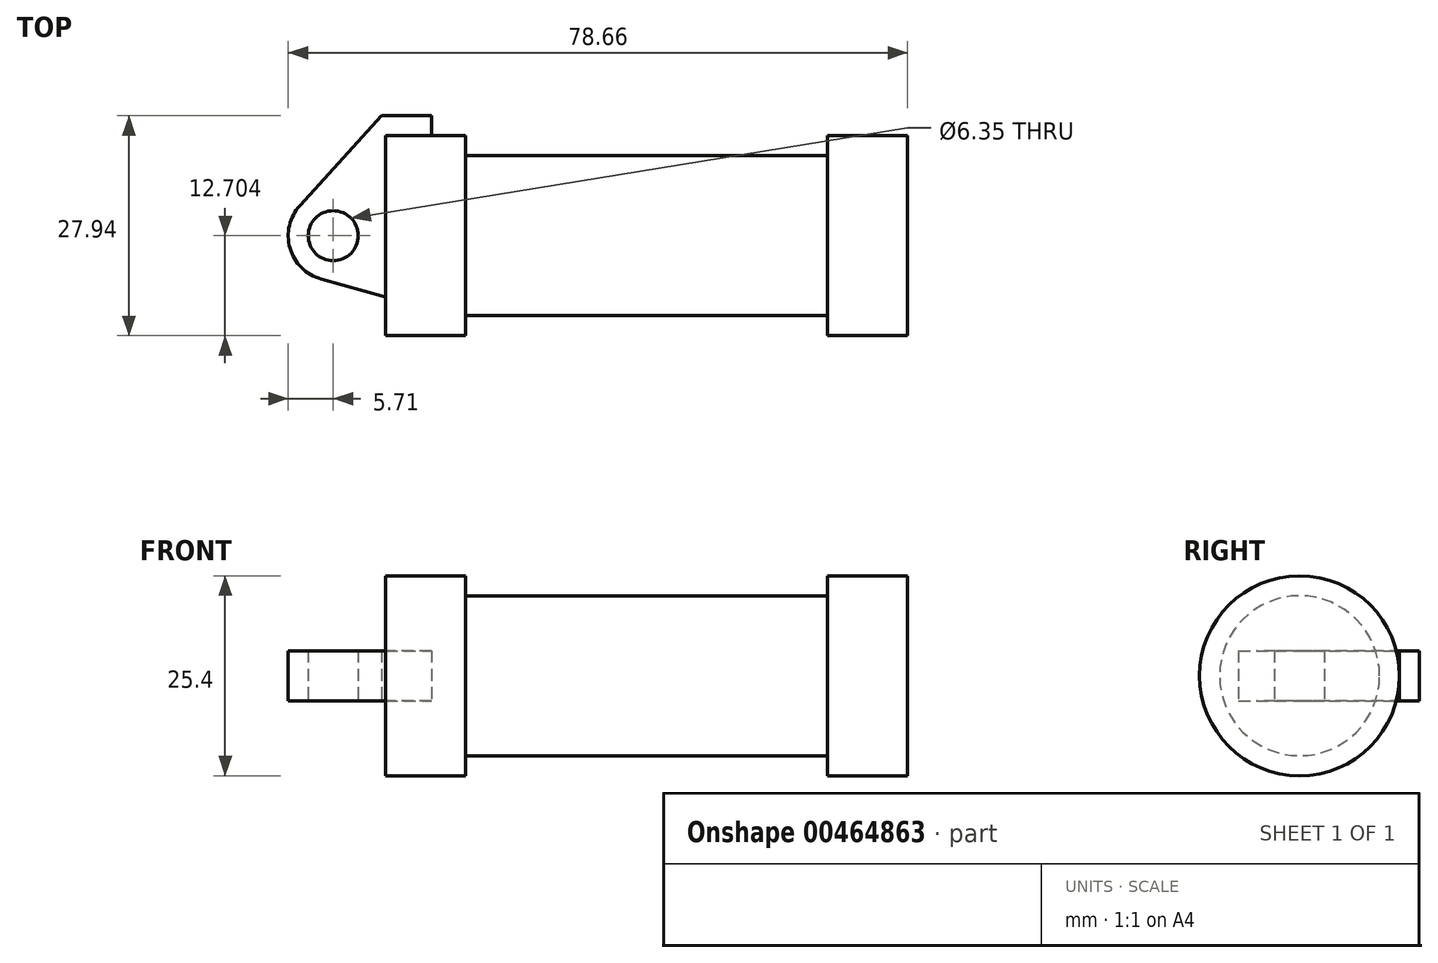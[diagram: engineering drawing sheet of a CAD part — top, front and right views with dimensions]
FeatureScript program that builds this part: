
annotation { "Feature Type Name" : "Feature", "Feature Type Description" : "" }
export const myFeature = defineFeature(function(context is Context, id is Id, definition is map)
    precondition{}
    {
        {
            var Q0;
            Q0=qCreatedBy(makeId("Top.planeOp"),FACE);
            var sketch = newSketch(context, id + "F0", { "sketchPlane" : qUnion([Q0])});
            skLineSegment(sketch, "E0", {"start": v(-28.27, -5.2) * mm, "end": v(-28.27, 7.5) * mm});
            skLineSegment(sketch, "E1", {"start": v(-28.27, 7.5) * mm, "end": v(-18.11, 7.5) * mm});
            skLineSegment(sketch, "E2", {"start": v(-18.11, 7.5) * mm, "end": v(-18.11, 4.95) * mm});
            skLineSegment(sketch, "E3", {"start": v(-18.11, 4.95) * mm, "end": v(27.86, 4.95) * mm});
            skLineSegment(sketch, "E4", {"start": v(27.86, 4.95) * mm, "end": v(27.86, 7.5) * mm});
            skLineSegment(sketch, "E5", {"start": v(27.86, 7.5) * mm, "end": v(38.02, 7.5) * mm});
            skLineSegment(sketch, "E6", {"start": v(38.02, 7.5) * mm, "end": v(38.02, -5.2) * mm});
            skLineSegment(sketch, "E7", {"start": v(38.02, -5.2) * mm, "end": v(-28.27, -5.2) * mm});
            skLineSegment(sketch, "E8", {"start": v(-22.43, 10.03) * mm, "end": v(-28.78, 10.03) * mm});
            skLineSegment(sketch, "E9", {"start": v(-28.78, 10.03) * mm, "end": v(-39.16, -1.36) * mm});
            skLineSegment(sketch, "E10", {"start": v(-28.27, -5.2) * mm, "end": v(-34.93, -5.2) * mm});
            skCircle(sketch, "E11", {"center": v(-34.93, -5.2) * mm, "radius": 5.72 * mm});
            skCircle(sketch, "E12", {"center": v(-34.93, -5.2) * mm, "radius": 3.18 * mm});
            skLineSegment(sketch, "E13", {"start": v(-22.43, 10.03) * mm, "end": v(-22.43, -14.6) * mm});
            skLineSegment(sketch, "E14", {"start": v(-22.43, -14.6) * mm, "end": v(-36.46, -10.71) * mm});
            skLineSegment(sketch, "E15", {"start": v(-28.27, -5.2) * mm, "end": v(-28.27, -12.98) * mm});
            skSolve(sketch);
        }
        {
            var Q0;
            {var subQ0=sQuery(id+"F0.wireOp",EDGE,"E2");Q0=makeQuery(id+"F0.imprint","IMPRINT",FACE,{"disambiguationData":[TD([[makeQuery(id+"F0.imprint","IMPRINT",EDGE,{"derivedFrom":subQ0}),-1.0]])]});}
            var Q1;
            {var subQ0=sQuery(id+"F0.wireOp",EDGE,"E0");Q1=makeQuery(id+"F0.imprint","IMPRINT",FACE,{"disambiguationData":[TD([[makeQuery(id+"F0.imprint","IMPRINT",EDGE,{"derivedFrom":subQ0}),-1.0]])]});}
            var Q2;
            Q2=sQuery(id+"F0.wireOp",EDGE,"E7");
            revolve(context, id + "F1", {"entities" : qUnion([Q0, Q1]), "axis" : qUnion([Q2]), "revolveType" : RevolveType.FULL});
        }
        {
            var Q0;
            {var subQ1=sQuery(id+"F0.wireOp",EDGE,"E0");Q0=makeQuery(id+"F0.imprint","IMPRINT",FACE,{"disambiguationData":[TD([[makeQuery(id+"F0.imprint","IMPRINT",EDGE,{"derivedFrom":subQ1}),1.0]])]});}
            var Q1;
            Q1=makeQuery(id+"F0.imprint","IMPRINT",FACE,{"disambiguationData":[TD([[makeQuery(id+"F0.imprint","IMPRINT",EDGE,{"derivedFrom":sQuery(id+"F0.wireOp",EDGE,"E12")}),-1.0]])]});
            var Q2;
            {var subQ0=sQuery(id+"F0.wireOp",EDGE,"E15");Q2=makeQuery(id+"F0.imprint","IMPRINT",FACE,{"disambiguationData":[TD([[makeQuery(id+"F0.imprint","IMPRINT",EDGE,{"derivedFrom":subQ0}),-1.0]])]});}
            extrude(context, id + "F2", {"entities" : qUnion([Q0, Q1, Q2]), "endBound" : BoundingType.SYMMETRIC, "depth" : 6.35 * mm});
        }
    });
